# Revit family: Skyfull_Janela-Oscilobatente-1-MOD
name_source: partatom
category: Windows
units: mm (PartAtom-declared; Revit-internal decimal feet)

## family parameters
Always vertical = Yes
Cut with Voids When Loaded = No
Host = Wall
OmniClass Number = 23.30.10.00
OmniClass Title = Doors
Room Calculation Point = No
Shared = No

## types (16) — shared parameters
Analytic Construction = <Nenhum>
Define Thermal Properties by = Schematic Type
Description = Janela com esquadria minimalista de alumínio, 1 Módulo
Developer = Blocks
Manufacturer = Ulimax&Co
Type Comments = Janela Oscilobatente Skyfull
URL = https://www.ulimax.com.br
URL Developer = www.BlocksRvt.com
URL Produto = https://www.skyfull.com.br
URL Template = https://www.skyfull.com.br
Visor = Skyfull - Glass - Transparent
Wall Closure = By host

## per-type parameters (varying)
| type | Caixilho | Height | Puxador | Rough Height | Rough Width | Width | b | c |
| Cinza - 0.60 x 1.20 | Skyfull - Metal - Chrome - 203-203-203 | 120 cm | Skyfull - Metal - Chrome - 203-203-203 | 129.14 cm | 69.14 cm | 60 cm | 120 cm | 60 cm |
| Cinza - 0.70 x 1.40 | Skyfull - Metal - Chrome - 203-203-203 | 140 cm | Skyfull - Metal - Chrome - 203-203-203 | 149.14 cm | 79.14 cm | 70 cm | 140 cm | 70 cm |
| Cinza - 0.80 x 1.60 | Skyfull - Metal - Chrome - 203-203-203 | 160 cm | Skyfull - Metal - Chrome - 203-203-203 | 169.14 cm | 89.14 cm | 80 cm | 160 cm | 80 cm |
| Cinza - 0.90 x 1.80 | Skyfull - Metal - Chrome - 203-203-203 | 180 cm | Skyfull - Metal - Chrome - 203-203-203 | 189.14 cm | 99.14 cm | 90 cm | 180 cm | 90 cm |
| Preto - 0.60 x 1.20 | Skyfull - Metal - Black - Matte - 15-15-15 | 120 cm | Skyfull - Metal - Black - Matte - 15-15-15 | 129.14 cm | 69.14 cm | 60 cm | 120 cm | 60 cm |
| Preto - 0.70 x 1.40 | Skyfull - Metal - Black - Matte - 15-15-15 | 140 cm | Skyfull - Metal - Black - Matte - 15-15-15 | 149.14 cm | 79.14 cm | 70 cm | 140 cm | 70 cm |
| Preto - 0.80 x 1.60 | Skyfull - Metal - Black - Matte - 15-15-15 | 160 cm | Skyfull - Metal - Black - Matte - 15-15-15 | 169.14 cm | 89.14 cm | 80 cm | 160 cm | 80 cm |
| Preto - 0.90 x 1.80 | Skyfull - Metal - Black - Matte - 15-15-15 | 180 cm | Skyfull - Metal - Black - Matte - 15-15-15 | 189.14 cm | 99.14 cm | 90 cm | 180 cm | 90 cm |
| Branco - 0.60 x 1.20 | Skyfull - Metal - White - Matte - 246-246-243 | 120 cm | Skyfull - Metal - White - Matte - 246-246-243 | 129.14 cm | 69.14 cm | 60 cm | 120 cm | 60 cm |
| Branco - 0.70 x 1.40 | Skyfull - Metal - White - Matte - 246-246-243 | 140 cm | Skyfull - Metal - White - Matte - 246-246-243 | 149.14 cm | 79.14 cm | 70 cm | 140 cm | 70 cm |
| Branco - 0.80 x 1.60 | Skyfull - Metal - White - Matte - 246-246-243 | 160 cm | Skyfull - Metal - White - Matte - 246-246-243 | 169.14 cm | 89.14 cm | 80 cm | 160 cm | 80 cm |
| Branco - 0.90 x 1.80 | Skyfull - Metal - White - Matte - 246-246-243 | 180 cm | Skyfull - Metal - White - Matte - 246-246-243 | 189.14 cm | 99.14 cm | 90 cm | 180 cm | 90 cm |
| Champanhe - 0.60 x 1.20 | Skyfull - Metal - Beige - Matte - 230-200-160 | 120 cm | Skyfull - Metal - Beige - Matte - 230-200-160 | 129.14 cm | 69.14 cm | 60 cm | 120 cm | 60 cm |
| Champanhe - 0.70 x 1.40 | Skyfull - Metal - Beige - Matte - 230-200-160 | 140 cm | Skyfull - Metal - Beige - Matte - 230-200-160 | 149.14 cm | 79.14 cm | 70 cm | 140 cm | 70 cm |
| Champanhe - 0.80 x 1.60 | Skyfull - Metal - Beige - Matte - 230-200-160 | 160 cm | Skyfull - Metal - Beige - Matte - 230-200-160 | 169.14 cm | 89.14 cm | 80 cm | 160 cm | 80 cm |
| Champanhe - 0.90 x 1.80 | Skyfull - Metal - Beige - Matte - 230-200-160 | 180 cm | Skyfull - Metal - Beige - Matte - 230-200-160 | 189.14 cm | 99.14 cm | 90 cm | 180 cm | 90 cm |
